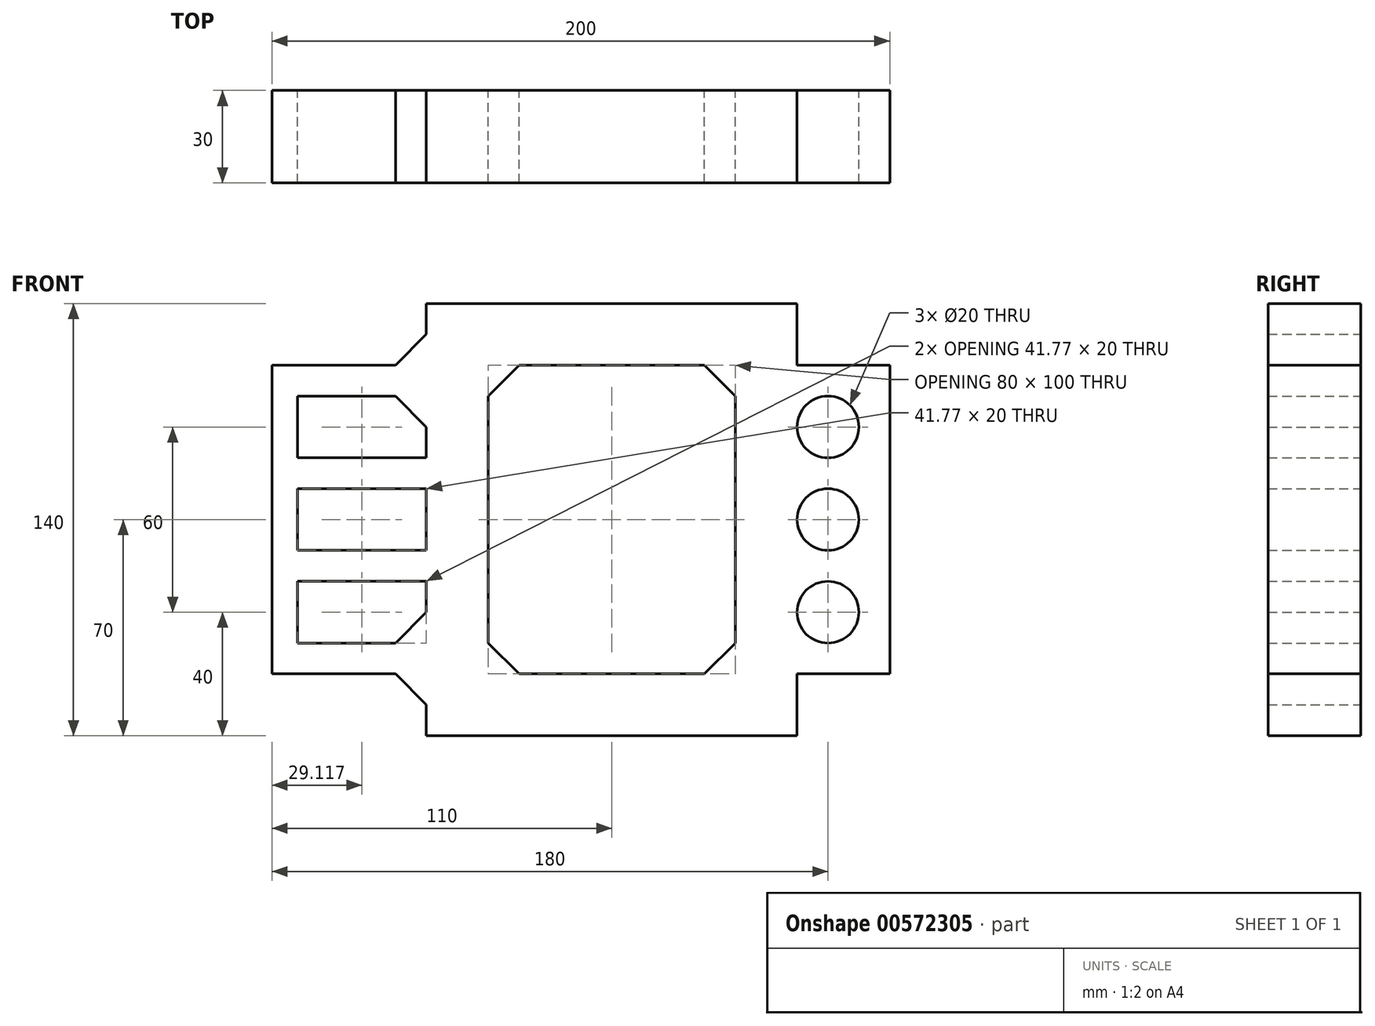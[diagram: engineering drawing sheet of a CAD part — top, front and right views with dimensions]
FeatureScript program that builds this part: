
annotation { "Feature Type Name" : "Feature", "Feature Type Description" : "" }
export const myFeature = defineFeature(function(context is Context, id is Id, definition is map)
    precondition{}
    {
        {
            var Q0;
            Q0=qCreatedBy(makeId("Front.planeOp"),FACE);
            var sketch = newSketch(context, id + "F0", { "sketchPlane" : qUnion([Q0])});
            skLineSegment(sketch, "E0", {"start": v(0, 0) * mm, "end": v(120, 0) * mm});
            skLineSegment(sketch, "E1", {"start": v(120, 0) * mm, "end": v(120, 20) * mm});
            skLineSegment(sketch, "E2", {"start": v(120, 20) * mm, "end": v(150, 20) * mm});
            skLineSegment(sketch, "E3", {"start": v(150, 20) * mm, "end": v(150, 120) * mm});
            skLineSegment(sketch, "E4", {"start": v(150, 120) * mm, "end": v(120, 120) * mm});
            skLineSegment(sketch, "E5", {"start": v(120, 120) * mm, "end": v(120, 140) * mm});
            skLineSegment(sketch, "E6", {"start": v(120, 140) * mm, "end": v(0, 140) * mm});
            skLineSegment(sketch, "E7", {"start": v(0, 140) * mm, "end": v(0, 130) * mm});
            skLineSegment(sketch, "E8", {"start": v(-19.49, 120) * mm, "end": v(-50, 120) * mm});
            skLineSegment(sketch, "E9", {"start": v(-50, 120) * mm, "end": v(-50, 20) * mm});
            skLineSegment(sketch, "E10", {"start": v(-50, 20) * mm, "end": v(-19.49, 20) * mm});
            skLineSegment(sketch, "E11", {"start": v(0, 10) * mm, "end": v(0, 0) * mm});
            skLineSegment(sketch, "E12", {"start": v(-19.49, 120) * mm, "end": v(-10, 120) * mm});
            skLineSegment(sketch, "E13", {"start": v(0, 130) * mm, "end": v(0, 140) * mm});
            skLineSegment(sketch, "E14", {"start": v(30, 120) * mm, "end": v(90, 120) * mm});
            skLineSegment(sketch, "E15", {"start": v(100, 110) * mm, "end": v(100, 30) * mm});
            skLineSegment(sketch, "E16", {"start": v(90, 20) * mm, "end": v(30, 20) * mm});
            skLineSegment(sketch, "E17", {"start": v(20, 30) * mm, "end": v(20, 110) * mm});
            skPoint(sketch, "E18.visualSharp", {"position": v(0, 120) * mm});
            skLineSegment(sketch, "E19", {"start": v(-10, 120) * mm, "end": v(0, 130) * mm});
            skPoint(sketch, "E20.visualSharp", {"position": v(0, 41.92) * mm});
            skLineSegment(sketch, "E21", {"start": v(-19.49, 20) * mm, "end": v(-10, 20) * mm});
            skLineSegment(sketch, "E22", {"start": v(0, 10) * mm, "end": v(0, 10) * mm});
            skPoint(sketch, "E23.visualSharp", {"position": v(0, 20) * mm});
            skLineSegment(sketch, "E24", {"start": v(-10, 20) * mm, "end": v(0, 10) * mm});
            skLineSegment(sketch, "E25", {"start": v(60, 20) * mm, "end": v(60, 0) * mm, "construction": true});
            skPoint(sketch, "E26.visualSharp", {"position": v(20, 120) * mm});
            skPoint(sketch, "E27.visualSharp", {"position": v(100, 120) * mm});
            skPoint(sketch, "E28.visualSharp", {"position": v(100, 20) * mm});
            skPoint(sketch, "E29.visualSharp", {"position": v(20, 20) * mm});
            skLineSegment(sketch, "E30", {"start": v(20, 110) * mm, "end": v(30, 120) * mm});
            skLineSegment(sketch, "E31", {"start": v(90, 120) * mm, "end": v(100, 110) * mm});
            skLineSegment(sketch, "E32", {"start": v(100, 30) * mm, "end": v(90, 20) * mm});
            skLineSegment(sketch, "E33", {"start": v(30, 20) * mm, "end": v(20, 30) * mm});
            skLineSegment(sketch, "E34.bottom", {"start": v(-41.77, 110) * mm, "end": v(-10, 110) * mm});
            skLineSegment(sketch, "E34.top", {"start": v(-41.77, 90) * mm, "end": v(0, 90) * mm});
            skLineSegment(sketch, "E34.left", {"start": v(-41.77, 110) * mm, "end": v(-41.77, 90) * mm});
            skLineSegment(sketch, "E34.right", {"start": v(0, 100) * mm, "end": v(0, 90) * mm});
            skLineSegment(sketch, "E35.bottom", {"start": v(-41.77, 80) * mm, "end": v(0, 80) * mm});
            skLineSegment(sketch, "E35.top", {"start": v(-41.77, 60) * mm, "end": v(0, 60) * mm});
            skLineSegment(sketch, "E35.left", {"start": v(-41.77, 80) * mm, "end": v(-41.77, 60) * mm});
            skLineSegment(sketch, "E35.right", {"start": v(0, 80) * mm, "end": v(0, 60) * mm});
            skLineSegment(sketch, "E36.bottom", {"start": v(-41.77, 50) * mm, "end": v(0, 50) * mm});
            skLineSegment(sketch, "E36.top", {"start": v(-41.77, 30) * mm, "end": v(-10, 30) * mm});
            skLineSegment(sketch, "E36.left", {"start": v(-41.77, 50) * mm, "end": v(-41.77, 30) * mm});
            skLineSegment(sketch, "E36.right", {"start": v(0, 50) * mm, "end": v(0, 40) * mm});
            skCircle(sketch, "E37", {"center": v(130, 100) * mm, "radius": 10 * mm});
            skCircle(sketch, "E38", {"center": v(130, 70) * mm, "radius": 10 * mm});
            skCircle(sketch, "E39", {"center": v(130, 40) * mm, "radius": 10 * mm});
            skPoint(sketch, "E40.visualSharp", {"position": v(0, 110) * mm});
            skPoint(sketch, "E41.visualSharp", {"position": v(0, 30) * mm});
            skLineSegment(sketch, "E42", {"start": v(0, 100) * mm, "end": v(-10, 110) * mm});
            skLineSegment(sketch, "E43", {"start": v(-10, 30) * mm, "end": v(0, 40) * mm});
            skSolve(sketch);
        }
        {
            var Q0;
            Q0 = qSketchRegion(id + "F0", true);
            extrude(context, id + "F1", {"entities" : qUnion([Q0]), "depth" : 30 * mm, "offsetDistance" : 25 * mm});
        }
    });
